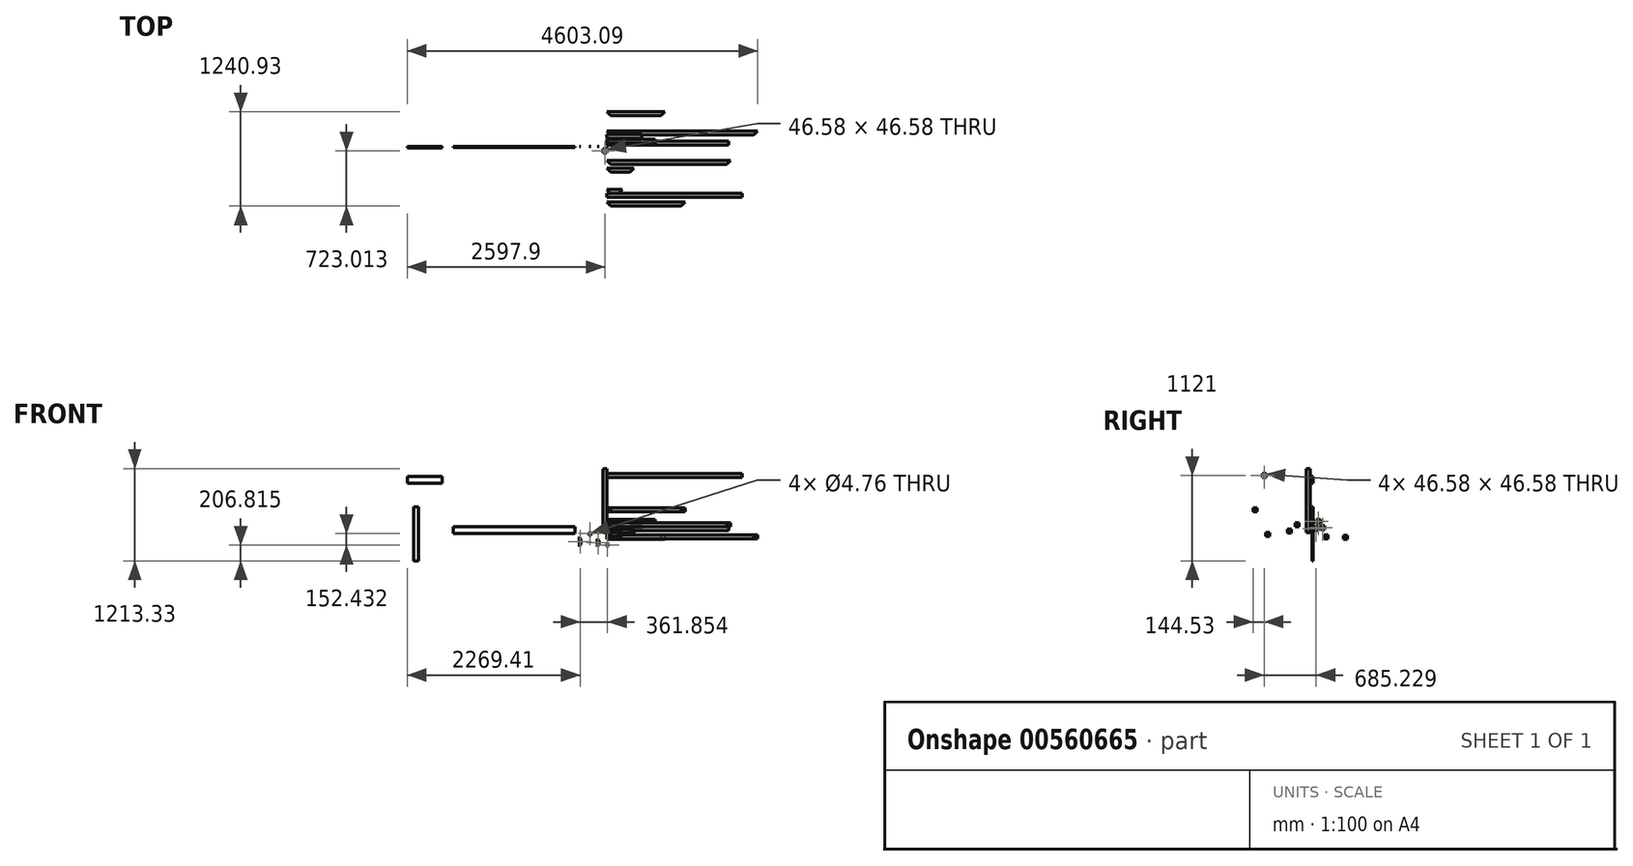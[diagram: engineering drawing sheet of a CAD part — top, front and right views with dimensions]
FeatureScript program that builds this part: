
annotation { "Feature Type Name" : "Feature", "Feature Type Description" : "" }
export const myFeature = defineFeature(function(context is Context, id is Id, definition is map)
    precondition{}
    {
        {
            var Q0;
            Q0=qCreatedBy(makeId("Top.planeOp"),FACE);
            var sketch = newSketch(context, id + "F0", { "sketchPlane" : qUnion([Q0])});
            skLineSegment(sketch, "E0.bottom", {"start": v(-49.39, -37.5) * mm, "end": v(1.41, -37.5) * mm});
            skLineSegment(sketch, "E0.top", {"start": v(-49.39, -88.3) * mm, "end": v(1.41, -88.3) * mm});
            skLineSegment(sketch, "E0.left", {"start": v(-49.39, -37.5) * mm, "end": v(-49.39, -88.3) * mm});
            skLineSegment(sketch, "E0.right", {"start": v(1.41, -37.5) * mm, "end": v(1.41, -88.3) * mm});
            skLineSegment(sketch, "E1.bottom", {"start": v(-47.28, -39.6) * mm, "end": v(-0.7, -39.6) * mm});
            skLineSegment(sketch, "E1.top", {"start": v(-47.28, -86.19) * mm, "end": v(-0.7, -86.19) * mm});
            skLineSegment(sketch, "E1.left", {"start": v(-47.28, -39.6) * mm, "end": v(-47.28, -86.19) * mm});
            skLineSegment(sketch, "E1.right", {"start": v(-0.7, -39.6) * mm, "end": v(-0.7, -86.19) * mm});
            skSolve(sketch);
        }
        {
            var Q0;
            Q0=makeQuery(id+"F0.imprint","IMPRINT",FACE,{"disambiguationData":[TD([[makeQuery(id+"F0.imprint","IMPRINT",EDGE,{"derivedFrom":sQuery(id+"F0.wireOp",EDGE,"E0.bottom")}),-1.0]])]});
            extrude(context, id + "F1", {"entities" : qUnion([Q0]), "depth" : 838.2 * mm, "offsetDistance" : 25.4 * mm});
        }
        {
            var Q0;
            Q0=qCreatedBy(makeId("Right.planeOp"),FACE);
            var sketch = newSketch(context, id + "F2", { "sketchPlane" : qUnion([Q0])});
            skLineSegment(sketch, "E2.bottom", {"start": v(18.45, 73.8) * mm, "end": v(69.25, 73.8) * mm});
            skLineSegment(sketch, "E2.top", {"start": v(18.45, 23) * mm, "end": v(69.25, 23) * mm});
            skLineSegment(sketch, "E2.left", {"start": v(18.45, 73.8) * mm, "end": v(18.45, 23) * mm});
            skLineSegment(sketch, "E2.right", {"start": v(69.25, 73.8) * mm, "end": v(69.25, 23) * mm});
            skLineSegment(sketch, "E3.bottom", {"start": v(20.56, 71.7) * mm, "end": v(67.14, 71.7) * mm});
            skLineSegment(sketch, "E3.top", {"start": v(20.56, 25.12) * mm, "end": v(67.14, 25.12) * mm});
            skLineSegment(sketch, "E3.left", {"start": v(20.56, 71.7) * mm, "end": v(20.56, 25.12) * mm});
            skLineSegment(sketch, "E3.right", {"start": v(67.14, 71.7) * mm, "end": v(67.14, 25.12) * mm});
            skSolve(sketch);
        }
        {
            var Q0;
            Q0=makeQuery(id+"F2.imprint","IMPRINT",FACE,{"disambiguationData":[TD([[makeQuery(id+"F2.imprint","IMPRINT",EDGE,{"derivedFrom":sQuery(id+"F2.wireOp",EDGE,"E2.bottom")}),-1.0]])]});
            extrude(context, id + "F3", {"entities" : qUnion([Q0]), "depth" : 1600.2 * mm, "offsetDistance" : 25.4 * mm});
        }
        {
            var Q0;
            Q0=qCreatedBy(makeId("Right.planeOp"),FACE);
            var sketch = newSketch(context, id + "F4", { "sketchPlane" : qUnion([Q0])});
            skLineSegment(sketch, "E4.bottom", {"start": v(104.32, 88.9) * mm, "end": v(155.12, 88.9) * mm});
            skLineSegment(sketch, "E4.top", {"start": v(104.32, 38.1) * mm, "end": v(155.12, 38.1) * mm});
            skLineSegment(sketch, "E4.left", {"start": v(104.32, 88.9) * mm, "end": v(104.32, 38.1) * mm});
            skLineSegment(sketch, "E4.right", {"start": v(155.12, 88.9) * mm, "end": v(155.12, 38.1) * mm});
            skLineSegment(sketch, "E5.bottom", {"start": v(106.43, 86.8) * mm, "end": v(153.01, 86.8) * mm});
            skLineSegment(sketch, "E5.top", {"start": v(106.43, 40.21) * mm, "end": v(153.01, 40.21) * mm});
            skLineSegment(sketch, "E5.left", {"start": v(106.43, 86.8) * mm, "end": v(106.43, 40.21) * mm});
            skLineSegment(sketch, "E5.right", {"start": v(153.01, 86.8) * mm, "end": v(153.01, 40.21) * mm});
            skSolve(sketch);
        }
        {
            var Q0;
            Q0=makeQuery(id+"F4.imprint","IMPRINT",FACE,{"disambiguationData":[TD([[makeQuery(id+"F4.imprint","IMPRINT",EDGE,{"derivedFrom":sQuery(id+"F4.wireOp",EDGE,"E4.bottom")}),-1.0]])]});
            extrude(context, id + "F5", {"entities" : qUnion([Q0]), "depth" : 457.2 * mm, "offsetDistance" : 25.4 * mm});
        }
        {
            var Q0;
            Q0=qCreatedBy(makeId("Right.planeOp"),FACE);
            var sketch = newSketch(context, id + "F6", { "sketchPlane" : qUnion([Q0])});
            skLineSegment(sketch, "E6.bottom", {"start": v(148.9, -31.37) * mm, "end": v(199.7, -31.37) * mm});
            skLineSegment(sketch, "E6.top", {"start": v(148.9, -82.17) * mm, "end": v(199.7, -82.17) * mm});
            skLineSegment(sketch, "E6.left", {"start": v(148.9, -31.37) * mm, "end": v(148.9, -82.17) * mm});
            skLineSegment(sketch, "E6.right", {"start": v(199.7, -31.37) * mm, "end": v(199.7, -82.17) * mm});
            skLineSegment(sketch, "E7.bottom", {"start": v(151, -33.48) * mm, "end": v(197.6, -33.48) * mm});
            skLineSegment(sketch, "E7.top", {"start": v(151, -80.07) * mm, "end": v(197.6, -80.07) * mm});
            skLineSegment(sketch, "E7.left", {"start": v(151, -33.48) * mm, "end": v(151, -80.07) * mm});
            skLineSegment(sketch, "E7.right", {"start": v(197.6, -33.48) * mm, "end": v(197.6, -80.07) * mm});
            skSolve(sketch);
        }
        {
            var Q0;
            Q0=makeQuery(id+"F6.imprint","IMPRINT",FACE,{"disambiguationData":[TD([[makeQuery(id+"F6.imprint","IMPRINT",EDGE,{"derivedFrom":sQuery(id+"F6.wireOp",EDGE,"E6.bottom")}),-1.0]])]});
            extrude(context, id + "F7", {"entities" : qUnion([Q0]), "depth" : 1981.2 * mm, "offsetDistance" : 25.4 * mm});
        }
        {
            var Q0;
            Q0=makeQuery(id+"F7.opExtrude","SWEPT_FACE",FACE,{"disambiguationData":[OSD([sQuery(id+"F6.wireOp",EDGE,"E6.bottom")])]});
            var sketch = newSketch(context, id + "F8", { "sketchPlane" : qUnion([Q0])});
            skLineSegment(sketch, "E8", {"start": v(1981.2, 199.7) * mm, "end": v(1930.4, 148.9) * mm});
            skLineSegment(sketch, "E9", {"start": v(1930.4, 148.9) * mm, "end": v(1981.2, 148.9) * mm});
            skLineSegment(sketch, "E10", {"start": v(1981.2, 148.9) * mm, "end": v(1981.2, 199.7) * mm});
            skLineSegment(sketch, "E11", {"start": v(0, 199.7) * mm, "end": v(0, 148.9) * mm});
            skLineSegment(sketch, "E12", {"start": v(0, 148.9) * mm, "end": v(50.8, 148.9) * mm});
            skLineSegment(sketch, "E13", {"start": v(50.8, 148.9) * mm, "end": v(0, 199.7) * mm});
            skSolve(sketch);
        }
        {
            var Q0;
            Q0=makeQuery(id+"F8.imprint","IMPRINT",FACE,{"disambiguationData":[TD([[makeQuery(id+"F8.imprint","IMPRINT",EDGE,{"derivedFrom":sQuery(id+"F8.wireOp",EDGE,"E8")}),1.0]])]});
            var Q1;
            Q1=makeQuery(id+"F8.imprint","IMPRINT",FACE,{"disambiguationData":[TD([[makeQuery(id+"F8.imprint","IMPRINT",EDGE,{"derivedFrom":sQuery(id+"F8.wireOp",EDGE,"E11")}),-1.0]])]});
            var Q2;
            Q2=makeQuery(id+"F7.opExtrude","SWEPT_FACE",FACE,{"disambiguationData":[OSD([sQuery(id+"F6.wireOp",EDGE,"E6.top")])]});
            extrude(context, id + "F9", {"entities" : qUnion([Q0, Q1]), "operationType" : NewBodyOperationType.REMOVE, "endBound" : BoundingType.UP_TO_SURFACE, "oppositeDirection" : true, "depth" : 25.4 * mm, "endBoundEntityFace" : qUnion([Q2]), "offsetDistance" : 25.4 * mm});
        }
        {
            var Q0;
            Q0=qCreatedBy(makeId("Right.planeOp"),FACE);
            var sketch = newSketch(context, id + "F10", { "sketchPlane" : qUnion([Q0])});
            skLineSegment(sketch, "E14.bottom", {"start": v(404.22, -37.96) * mm, "end": v(455.02, -37.96) * mm});
            skLineSegment(sketch, "E14.top", {"start": v(404.22, -88.76) * mm, "end": v(455.02, -88.76) * mm});
            skLineSegment(sketch, "E14.left", {"start": v(404.22, -37.96) * mm, "end": v(404.22, -88.76) * mm});
            skLineSegment(sketch, "E14.right", {"start": v(455.02, -37.96) * mm, "end": v(455.02, -88.76) * mm});
            skLineSegment(sketch, "E15.bottom", {"start": v(406.33, -40.07) * mm, "end": v(452.92, -40.07) * mm});
            skLineSegment(sketch, "E15.top", {"start": v(406.33, -86.66) * mm, "end": v(452.92, -86.66) * mm});
            skLineSegment(sketch, "E15.left", {"start": v(406.33, -40.07) * mm, "end": v(406.33, -86.66) * mm});
            skLineSegment(sketch, "E15.right", {"start": v(452.92, -40.07) * mm, "end": v(452.92, -86.66) * mm});
            skSolve(sketch);
        }
        {
            var Q0;
            Q0=makeQuery(id+"F10.imprint","IMPRINT",FACE,{"disambiguationData":[TD([[makeQuery(id+"F10.imprint","IMPRINT",EDGE,{"derivedFrom":sQuery(id+"F10.wireOp",EDGE,"E14.bottom")}),-1.0]])]});
            extrude(context, id + "F11", {"entities" : qUnion([Q0]), "depth" : 762 * mm, "offsetDistance" : 25.4 * mm});
        }
        {
            var Q0;
            Q0=makeQuery(id+"F11.opExtrude","SWEPT_FACE",FACE,{"disambiguationData":[OSD([sQuery(id+"F10.wireOp",EDGE,"E14.bottom")])]});
            var sketch = newSketch(context, id + "F12", { "sketchPlane" : qUnion([Q0])});
            skLineSegment(sketch, "E16", {"start": v(0, 455.02) * mm, "end": v(0, 404.22) * mm});
            skLineSegment(sketch, "E17", {"start": v(0, 404.22) * mm, "end": v(50.8, 404.22) * mm});
            skLineSegment(sketch, "E18", {"start": v(50.8, 404.22) * mm, "end": v(0, 455.02) * mm});
            skLineSegment(sketch, "E19", {"start": v(762, 455.02) * mm, "end": v(762, 404.22) * mm});
            skLineSegment(sketch, "E20", {"start": v(762, 404.22) * mm, "end": v(711.2, 404.22) * mm});
            skLineSegment(sketch, "E21", {"start": v(711.2, 404.22) * mm, "end": v(762, 455.02) * mm});
            skSolve(sketch);
        }
        {
            var Q0;
            Q0=makeQuery(id+"F12.imprint","IMPRINT",FACE,{"disambiguationData":[TD([[makeQuery(id+"F12.imprint","IMPRINT",EDGE,{"derivedFrom":sQuery(id+"F12.wireOp",EDGE,"E16")}),-1.0]])]});
            var Q1;
            Q1=makeQuery(id+"F12.imprint","IMPRINT",FACE,{"disambiguationData":[TD([[makeQuery(id+"F12.imprint","IMPRINT",EDGE,{"derivedFrom":sQuery(id+"F12.wireOp",EDGE,"E19")}),1.0]])]});
            var Q2;
            Q2=makeQuery(id+"F11.opExtrude","SWEPT_FACE",FACE,{"disambiguationData":[OSD([sQuery(id+"F10.wireOp",EDGE,"E14.top")])]});
            extrude(context, id + "F13", {"entities" : qUnion([Q0, Q1]), "operationType" : NewBodyOperationType.REMOVE, "endBound" : BoundingType.UP_TO_SURFACE, "oppositeDirection" : true, "depth" : 25.4 * mm, "endBoundEntityFace" : qUnion([Q2]), "offsetDistance" : 25.4 * mm});
        }
        {
            var Q0;
            Q0=qCreatedBy(makeId("Front.planeOp"),FACE);
            var sketch = newSketch(context, id + "F14", { "sketchPlane" : qUnion([Q0])});
            skLineSegment(sketch, "E22", {"start": v(-129.12, -84.35) * mm, "end": v(-129.12, -185.95) * mm});
            skLineSegment(sketch, "E23", {"start": v(-129.12, -185.95) * mm, "end": v(-103.72, -160.55) * mm});
            skLineSegment(sketch, "E24", {"start": v(-103.72, -160.55) * mm, "end": v(-103.72, -109.75) * mm});
            skLineSegment(sketch, "E25", {"start": v(-103.72, -109.75) * mm, "end": v(-129.12, -84.35) * mm});
            skCircle(sketch, "E26", {"center": v(-116.42, -135.15) * mm, "radius": 2.38 * mm});
            skSolve(sketch);
        }
        {
            var Q0;
            Q0=makeQuery(id+"F14.imprint","IMPRINT",FACE,{"disambiguationData":[TD([[makeQuery(id+"F14.imprint","IMPRINT",EDGE,{"derivedFrom":sQuery(id+"F14.wireOp",EDGE,"E22")}),1.0]])]});
            extrude(context, id + "F15", {"entities" : qUnion([Q0]), "depth" : 3.17 * mm, "offsetDistance" : 25.4 * mm});
        }
        {
            var Q0;
            Q0=qCreatedBy(makeId("Front.planeOp"),FACE);
            var sketch = newSketch(context, id + "F16", { "sketchPlane" : qUnion([Q0])});
            skLineSegment(sketch, "E27.bottom", {"start": v(-3.32, -155.62) * mm, "end": v(22.08, -155.62) * mm});
            skLineSegment(sketch, "E27.top", {"start": v(-3.32, -181.02) * mm, "end": v(22.08, -181.02) * mm});
            skLineSegment(sketch, "E27.left", {"start": v(-3.32, -155.62) * mm, "end": v(-3.32, -181.02) * mm});
            skLineSegment(sketch, "E27.right", {"start": v(22.08, -155.62) * mm, "end": v(22.08, -181.02) * mm});
            skCircle(sketch, "E28", {"center": v(9.38, -168.32) * mm, "radius": 2.38 * mm});
            skSolve(sketch);
        }
        {
            var Q0;
            Q0=makeQuery(id+"F16.imprint","IMPRINT",FACE,{"disambiguationData":[TD([[makeQuery(id+"F16.imprint","IMPRINT",EDGE,{"derivedFrom":sQuery(id+"F16.wireOp",EDGE,"E27.bottom")}),-1.0]])]});
            extrude(context, id + "F17", {"entities" : qUnion([Q0]), "depth" : 3.17 * mm, "offsetDistance" : 25.4 * mm});
        }
        {
            var Q0;
            Q0=qCreatedBy(makeId("Front.planeOp"),FACE);
            var sketch = newSketch(context, id + "F18", { "sketchPlane" : qUnion([Q0])});
            skLineSegment(sketch, "E29.bottom", {"start": v(-2020.95, 72.64) * mm, "end": v(-420.75, 72.64) * mm});
            skLineSegment(sketch, "E29.top", {"start": v(-2020.95, -16.26) * mm, "end": v(-420.75, -16.26) * mm});
            skLineSegment(sketch, "E29.left", {"start": v(-2020.95, 72.64) * mm, "end": v(-2020.95, -16.26) * mm});
            skLineSegment(sketch, "E29.right", {"start": v(-420.75, 72.64) * mm, "end": v(-420.75, -16.26) * mm});
            skSolve(sketch);
        }
        {
            var Q0;
            Q0=makeQuery(id+"F18.imprint","IMPRINT",FACE,{"disambiguationData":[TD([[makeQuery(id+"F18.imprint","IMPRINT",EDGE,{"derivedFrom":sQuery(id+"F18.wireOp",EDGE,"E29.bottom")}),-1.0]])]});
            extrude(context, id + "F19", {"entities" : qUnion([Q0]), "depth" : 12.7 * mm, "offsetDistance" : 25.4 * mm});
        }
        {
            var Q0;
            Q0=qCreatedBy(makeId("Front.planeOp"),FACE);
            var sketch = newSketch(context, id + "F20", { "sketchPlane" : qUnion([Q0])});
            skLineSegment(sketch, "E30.bottom", {"start": v(-2539.62, 336.07) * mm, "end": v(-2476.12, 336.07) * mm});
            skLineSegment(sketch, "E30.top", {"start": v(-2539.62, -375.13) * mm, "end": v(-2476.12, -375.13) * mm});
            skLineSegment(sketch, "E30.left", {"start": v(-2539.62, 336.07) * mm, "end": v(-2539.62, -375.13) * mm});
            skLineSegment(sketch, "E30.right", {"start": v(-2476.12, 336.07) * mm, "end": v(-2476.12, -375.13) * mm});
            skSolve(sketch);
        }
        {
            var Q0;
            Q0=makeQuery(id+"F20.imprint","IMPRINT",FACE,{"disambiguationData":[TD([[makeQuery(id+"F20.imprint","IMPRINT",EDGE,{"derivedFrom":sQuery(id+"F20.wireOp",EDGE,"E30.bottom")}),-1.0]])]});
            extrude(context, id + "F21", {"entities" : qUnion([Q0]), "depth" : 12.7 * mm, "offsetDistance" : 25.4 * mm});
        }
        {
            var Q0;
            Q0=qCreatedBy(makeId("Right.planeOp"),FACE);
            var sketch = newSketch(context, id + "F22", { "sketchPlane" : qUnion([Q0])});
            skLineSegment(sketch, "E31.bottom", {"start": v(-336.46, 42.41) * mm, "end": v(-285.66, 42.41) * mm});
            skLineSegment(sketch, "E31.top", {"start": v(-336.46, -8.39) * mm, "end": v(-285.66, -8.39) * mm});
            skLineSegment(sketch, "E31.left", {"start": v(-336.46, 42.41) * mm, "end": v(-336.46, -8.39) * mm});
            skLineSegment(sketch, "E31.right", {"start": v(-285.66, 42.41) * mm, "end": v(-285.66, -8.39) * mm});
            skLineSegment(sketch, "E32.bottom", {"start": v(-334.35, 40.3) * mm, "end": v(-287.76, 40.3) * mm});
            skLineSegment(sketch, "E32.top", {"start": v(-334.35, -6.28) * mm, "end": v(-287.76, -6.28) * mm});
            skLineSegment(sketch, "E32.left", {"start": v(-334.35, 40.3) * mm, "end": v(-334.35, -6.28) * mm});
            skLineSegment(sketch, "E32.right", {"start": v(-287.76, 40.3) * mm, "end": v(-287.76, -6.28) * mm});
            skSolve(sketch);
        }
        {
            var Q0;
            Q0=makeQuery(id+"F22.imprint","IMPRINT",FACE,{"disambiguationData":[TD([[makeQuery(id+"F22.imprint","IMPRINT",EDGE,{"derivedFrom":sQuery(id+"F22.wireOp",EDGE,"E31.bottom")}),-1.0]])]});
            extrude(context, id + "F23", {"entities" : qUnion([Q0]), "depth" : 355.6 * mm, "offsetDistance" : 25.4 * mm});
        }
        {
            var Q0;
            Q0=makeQuery(id+"F23.opExtrude","CAP_EDGE",EDGE,{"disambiguationData":[OSD([sQuery(id+"F22.wireOp",EDGE,"E31.left")])],"isStart":false});
            var Q1;
            Q1=makeQuery(id+"F23.opExtrude","CAP_EDGE",EDGE,{"disambiguationData":[OSD([sQuery(id+"F22.wireOp",EDGE,"E31.left")])],"isStart":true});
            chamfer(context, id + "F24", {"entities" : qUnion([Q0, Q1]), "width" : 50.8 * mm, "tangentPropagation" : true});
        }
        {
            var Q0;
            Q0=qCreatedBy(makeId("Right.planeOp"),FACE);
            var sketch = newSketch(context, id + "F25", { "sketchPlane" : qUnion([Q0])});
            skLineSegment(sketch, "E33.bottom", {"start": v(-234.8, 122.1) * mm, "end": v(-184, 122.1) * mm});
            skLineSegment(sketch, "E33.top", {"start": v(-234.8, 71.3) * mm, "end": v(-184, 71.3) * mm});
            skLineSegment(sketch, "E33.left", {"start": v(-234.8, 122.1) * mm, "end": v(-234.8, 71.3) * mm});
            skLineSegment(sketch, "E33.right", {"start": v(-184, 122.1) * mm, "end": v(-184, 71.3) * mm});
            skLineSegment(sketch, "E34.bottom", {"start": v(-232.7, 119.98) * mm, "end": v(-186.11, 119.98) * mm});
            skLineSegment(sketch, "E34.top", {"start": v(-232.7, 73.4) * mm, "end": v(-186.11, 73.4) * mm});
            skLineSegment(sketch, "E34.left", {"start": v(-232.7, 119.98) * mm, "end": v(-232.7, 73.4) * mm});
            skLineSegment(sketch, "E34.right", {"start": v(-186.11, 119.98) * mm, "end": v(-186.11, 73.4) * mm});
            skSolve(sketch);
        }
        {
            var Q0;
            Q0=makeQuery(id+"F25.imprint","IMPRINT",FACE,{"disambiguationData":[TD([[makeQuery(id+"F25.imprint","IMPRINT",EDGE,{"derivedFrom":sQuery(id+"F25.wireOp",EDGE,"E33.bottom")}),-1.0]])]});
            extrude(context, id + "F26", {"entities" : qUnion([Q0]), "depth" : 1625.6 * mm, "offsetDistance" : 25.4 * mm});
        }
        {
            var Q0;
            Q0=makeQuery(id+"F26.opExtrude","CAP_EDGE",EDGE,{"disambiguationData":[OSD([sQuery(id+"F25.wireOp",EDGE,"E33.left")])],"isStart":true});
            var Q1;
            Q1=makeQuery(id+"F26.opExtrude","CAP_EDGE",EDGE,{"disambiguationData":[OSD([sQuery(id+"F25.wireOp",EDGE,"E33.left")])],"isStart":false});
            chamfer(context, id + "F27", {"entities" : qUnion([Q0, Q1]), "width" : 50.8 * mm, "tangentPropagation" : true});
        }
        {
            var Q0;
            Q0=qCreatedBy(makeId("Right.planeOp"),FACE);
            var sketch = newSketch(context, id + "F28", { "sketchPlane" : qUnion([Q0])});
            skLineSegment(sketch, "E35.bottom", {"start": v(-620.76, -3.73) * mm, "end": v(-569.96, -3.73) * mm});
            skLineSegment(sketch, "E35.top", {"start": v(-620.76, -54.53) * mm, "end": v(-569.96, -54.53) * mm});
            skLineSegment(sketch, "E35.left", {"start": v(-620.76, -3.73) * mm, "end": v(-620.76, -54.53) * mm});
            skLineSegment(sketch, "E35.right", {"start": v(-569.96, -3.73) * mm, "end": v(-569.96, -54.53) * mm});
            skLineSegment(sketch, "E36.bottom", {"start": v(-618.65, -5.83) * mm, "end": v(-572.07, -5.83) * mm});
            skLineSegment(sketch, "E36.top", {"start": v(-618.65, -52.42) * mm, "end": v(-572.07, -52.42) * mm});
            skLineSegment(sketch, "E36.left", {"start": v(-618.65, -5.83) * mm, "end": v(-618.65, -52.42) * mm});
            skLineSegment(sketch, "E36.right", {"start": v(-572.07, -5.83) * mm, "end": v(-572.07, -52.42) * mm});
            skSolve(sketch);
        }
        {
            var Q0;
            Q0=makeQuery(id+"F28.imprint","IMPRINT",FACE,{"disambiguationData":[TD([[makeQuery(id+"F28.imprint","IMPRINT",EDGE,{"derivedFrom":sQuery(id+"F28.wireOp",EDGE,"E35.bottom")}),-1.0]])]});
            extrude(context, id + "F29", {"entities" : qUnion([Q0]), "depth" : 203.2 * mm, "offsetDistance" : 25.4 * mm});
        }
        {
            var Q0;
            Q0=makeQuery(id+"F29.opExtrude","CAP_EDGE",EDGE,{"disambiguationData":[OSD([sQuery(id+"F28.wireOp",EDGE,"E35.left")])],"isStart":false});
            var Q1;
            Q1=makeQuery(id+"F29.opExtrude","CAP_EDGE",EDGE,{"disambiguationData":[OSD([sQuery(id+"F28.wireOp",EDGE,"E35.left")])],"isStart":true});
            chamfer(context, id + "F30", {"entities" : qUnion([Q0, Q1]), "width" : 50.8 * mm, "tangentPropagation" : true});
        }
        {
            var Q0;
            Q0=qCreatedBy(makeId("Front.planeOp"),FACE);
            var sketch = newSketch(context, id + "F31", { "sketchPlane" : qUnion([Q0])});
            skLineSegment(sketch, "E37", {"start": v(-365.18, -57.43) * mm, "end": v(-365.18, -184.43) * mm});
            skLineSegment(sketch, "E38", {"start": v(-365.18, -184.43) * mm, "end": v(-339.78, -159.03) * mm});
            skLineSegment(sketch, "E39", {"start": v(-339.78, -159.03) * mm, "end": v(-339.78, -82.83) * mm});
            skLineSegment(sketch, "E40", {"start": v(-339.78, -82.83) * mm, "end": v(-365.18, -57.43) * mm});
            skCircle(sketch, "E41", {"center": v(-352.48, -120.93) * mm, "radius": 2.38 * mm});
            skSolve(sketch);
        }
        {
            var Q0;
            Q0=makeQuery(id+"F31.imprint","IMPRINT",FACE,{"disambiguationData":[TD([[makeQuery(id+"F31.imprint","IMPRINT",EDGE,{"derivedFrom":sQuery(id+"F31.wireOp",EDGE,"E37")}),1.0]])]});
            extrude(context, id + "F32", {"entities" : qUnion([Q0]), "depth" : 3.17 * mm, "offsetDistance" : 25.4 * mm});
        }
        {
            var Q0;
            Q0=qCreatedBy(makeId("Front.planeOp"),FACE);
            var sketch = newSketch(context, id + "F33", { "sketchPlane" : qUnion([Q0])});
            skLineSegment(sketch, "E42.bottom", {"start": v(-235.47, -3.18) * mm, "end": v(-210.07, -3.18) * mm});
            skLineSegment(sketch, "E42.top", {"start": v(-235.47, -41.28) * mm, "end": v(-210.07, -41.28) * mm});
            skLineSegment(sketch, "E42.left", {"start": v(-235.47, -3.18) * mm, "end": v(-235.47, -41.28) * mm});
            skLineSegment(sketch, "E42.right", {"start": v(-210.07, -3.18) * mm, "end": v(-210.07, -41.28) * mm});
            skCircle(sketch, "E43", {"center": v(-222.77, -15.88) * mm, "radius": 2.38 * mm});
            skSolve(sketch);
        }
        {
            var Q0;
            Q0=makeQuery(id+"F33.imprint","IMPRINT",FACE,{"disambiguationData":[TD([[makeQuery(id+"F33.imprint","IMPRINT",EDGE,{"derivedFrom":sQuery(id+"F33.wireOp",EDGE,"E42.bottom")}),-1.0]])]});
            extrude(context, id + "F34", {"entities" : qUnion([Q0]), "depth" : 3.17 * mm, "offsetDistance" : 25.4 * mm});
        }
        {
            var Q0;
            Q0=qCreatedBy(makeId("Front.planeOp"),FACE);
            var sketch = newSketch(context, id + "F35", { "sketchPlane" : qUnion([Q0])});
            skLineSegment(sketch, "E44.bottom", {"start": v(-2621.89, 732.43) * mm, "end": v(-2164.69, 732.43) * mm});
            skLineSegment(sketch, "E44.top", {"start": v(-2621.89, 643.53) * mm, "end": v(-2164.69, 643.53) * mm});
            skLineSegment(sketch, "E44.left", {"start": v(-2621.89, 732.43) * mm, "end": v(-2621.89, 643.53) * mm});
            skLineSegment(sketch, "E44.right", {"start": v(-2164.69, 732.43) * mm, "end": v(-2164.69, 643.53) * mm});
            skSolve(sketch);
        }
        {
            var Q0;
            Q0=makeQuery(id+"F35.imprint","IMPRINT",FACE,{"disambiguationData":[TD([[makeQuery(id+"F35.imprint","IMPRINT",EDGE,{"derivedFrom":sQuery(id+"F35.wireOp",EDGE,"E44.bottom")}),-1.0]])]});
            extrude(context, id + "F36", {"entities" : qUnion([Q0]), "depth" : 19.05 * mm, "offsetDistance" : 25.4 * mm});
        }
        {
            var Q0;
            Q0=qCreatedBy(makeId("Right.planeOp"),FACE);
            var sketch = newSketch(context, id + "F37", { "sketchPlane" : qUnion([Q0])});
            skLineSegment(sketch, "E45.bottom", {"start": v(-785.9, 324.48) * mm, "end": v(-735.1, 324.48) * mm});
            skLineSegment(sketch, "E45.top", {"start": v(-785.9, 273.68) * mm, "end": v(-735.1, 273.68) * mm});
            skLineSegment(sketch, "E45.left", {"start": v(-785.9, 324.48) * mm, "end": v(-785.9, 273.68) * mm});
            skLineSegment(sketch, "E45.right", {"start": v(-735.1, 324.48) * mm, "end": v(-735.1, 273.68) * mm});
            skLineSegment(sketch, "E46.bottom", {"start": v(-783.8, 322.37) * mm, "end": v(-737.22, 322.37) * mm});
            skLineSegment(sketch, "E46.top", {"start": v(-783.8, 275.8) * mm, "end": v(-737.22, 275.8) * mm});
            skLineSegment(sketch, "E46.left", {"start": v(-783.8, 322.37) * mm, "end": v(-783.8, 275.8) * mm});
            skLineSegment(sketch, "E46.right", {"start": v(-737.22, 322.37) * mm, "end": v(-737.22, 275.8) * mm});
            skSolve(sketch);
        }
        {
            var Q0;
            Q0=makeQuery(id+"F37.imprint","IMPRINT",FACE,{"disambiguationData":[TD([[makeQuery(id+"F37.imprint","IMPRINT",EDGE,{"derivedFrom":sQuery(id+"F37.wireOp",EDGE,"E45.bottom")}),-1.0]])]});
            extrude(context, id + "F38", {"entities" : qUnion([Q0]), "depth" : 1028.7 * mm, "offsetDistance" : 25.4 * mm});
        }
        {
            var Q0;
            Q0=makeQuery(id+"F38.opExtrude","CAP_EDGE",EDGE,{"disambiguationData":[OSD([sQuery(id+"F37.wireOp",EDGE,"E45.left")])],"isStart":false});
            var Q1;
            Q1=makeQuery(id+"F38.opExtrude","CAP_EDGE",EDGE,{"disambiguationData":[OSD([sQuery(id+"F37.wireOp",EDGE,"E45.left")])],"isStart":true});
            chamfer(context, id + "F39", {"entities" : qUnion([Q0, Q1]), "width" : 50.8 * mm, "tangentPropagation" : true});
        }
        {
            var Q0;
            Q0=qCreatedBy(makeId("Right.planeOp"),FACE);
            var sketch = newSketch(context, id + "F40", { "sketchPlane" : qUnion([Q0])});
            skLineSegment(sketch, "E47.bottom", {"start": v(44.48, 167.56) * mm, "end": v(95.28, 167.56) * mm});
            skLineSegment(sketch, "E47.top", {"start": v(44.48, 116.76) * mm, "end": v(95.28, 116.76) * mm});
            skLineSegment(sketch, "E47.left", {"start": v(44.48, 167.56) * mm, "end": v(44.48, 116.76) * mm});
            skLineSegment(sketch, "E47.right", {"start": v(95.28, 167.56) * mm, "end": v(95.28, 116.76) * mm});
            skLineSegment(sketch, "E48.bottom", {"start": v(46.6, 165.45) * mm, "end": v(93.17, 165.45) * mm});
            skLineSegment(sketch, "E48.top", {"start": v(46.6, 118.87) * mm, "end": v(93.17, 118.87) * mm});
            skLineSegment(sketch, "E48.left", {"start": v(46.6, 165.45) * mm, "end": v(46.6, 118.87) * mm});
            skLineSegment(sketch, "E48.right", {"start": v(93.17, 165.45) * mm, "end": v(93.17, 118.87) * mm});
            skSolve(sketch);
        }
        {
            var Q0;
            Q0=makeQuery(id+"F40.imprint","IMPRINT",FACE,{"disambiguationData":[TD([[makeQuery(id+"F40.imprint","IMPRINT",EDGE,{"derivedFrom":sQuery(id+"F40.wireOp",EDGE,"E47.bottom")}),-1.0]])]});
            extrude(context, id + "F41", {"entities" : qUnion([Q0]), "depth" : 635 * mm, "offsetDistance" : 25.4 * mm});
        }
        {
            var Q0;
            Q0=qCreatedBy(makeId("Right.planeOp"),FACE);
            var sketch = newSketch(context, id + "F42", { "sketchPlane" : qUnion([Q0])});
            skLineSegment(sketch, "E49.bottom", {"start": v(-666.78, 771.27) * mm, "end": v(-615.98, 771.27) * mm});
            skLineSegment(sketch, "E49.top", {"start": v(-666.78, 720.47) * mm, "end": v(-615.98, 720.47) * mm});
            skLineSegment(sketch, "E49.left", {"start": v(-666.78, 771.27) * mm, "end": v(-666.78, 720.47) * mm});
            skLineSegment(sketch, "E49.right", {"start": v(-615.98, 771.27) * mm, "end": v(-615.98, 720.47) * mm});
            skLineSegment(sketch, "E50.bottom", {"start": v(-664.67, 769.16) * mm, "end": v(-618.09, 769.16) * mm});
            skLineSegment(sketch, "E50.top", {"start": v(-664.67, 722.58) * mm, "end": v(-618.09, 722.58) * mm});
            skLineSegment(sketch, "E50.left", {"start": v(-664.67, 769.16) * mm, "end": v(-664.67, 722.58) * mm});
            skLineSegment(sketch, "E50.right", {"start": v(-618.09, 769.16) * mm, "end": v(-618.09, 722.58) * mm});
            skSolve(sketch);
        }
        {
            var Q0;
            Q0=makeQuery(id+"F42.imprint","IMPRINT",FACE,{"disambiguationData":[TD([[makeQuery(id+"F42.imprint","IMPRINT",EDGE,{"derivedFrom":sQuery(id+"F42.wireOp",EDGE,"E49.bottom")}),-1.0]])]});
            extrude(context, id + "F43", {"entities" : qUnion([Q0]), "depth" : 1778 * mm, "offsetDistance" : 25.4 * mm});
        }
    });
